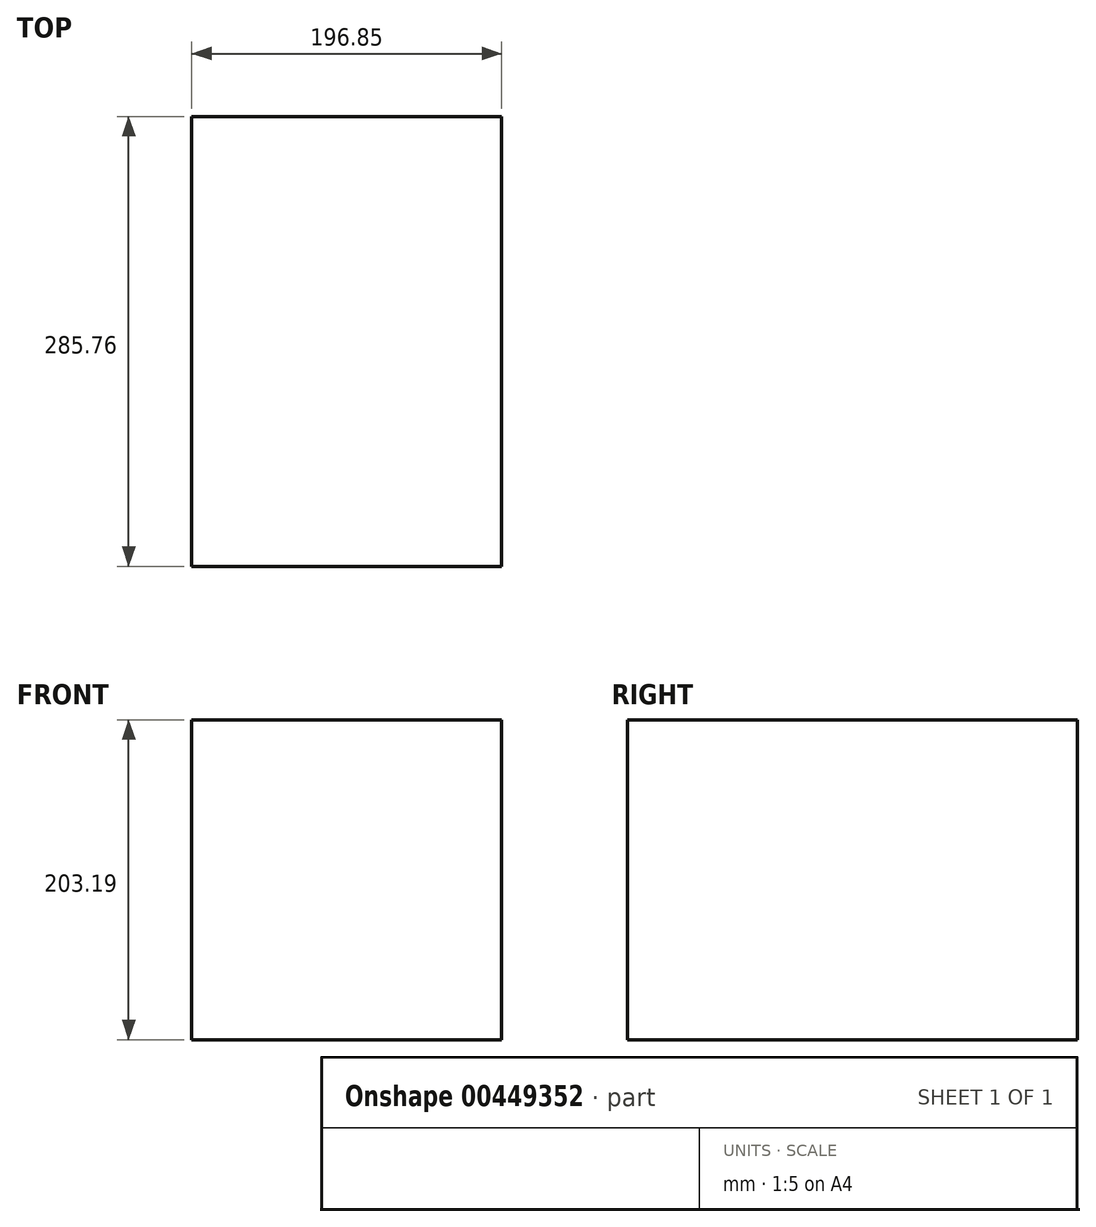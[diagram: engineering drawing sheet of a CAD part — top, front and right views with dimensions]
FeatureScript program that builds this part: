
annotation { "Feature Type Name" : "Feature", "Feature Type Description" : "" }
export const myFeature = defineFeature(function(context is Context, id is Id, definition is map)
    precondition{}
    {
        {
            var Q0;
            Q0=qCreatedBy(makeId("Front.planeOp"),FACE);
            var sketch = newSketch(context, id + "F0", { "sketchPlane" : qUnion([Q0])});
            skLineSegment(sketch, "E0.bottom", {"start": v(-92.08, 98.42) * mm, "end": v(104.78, 98.42) * mm});
            skLineSegment(sketch, "E0.top", {"start": v(-92.08, -104.78) * mm, "end": v(104.78, -104.78) * mm});
            skLineSegment(sketch, "E0.left", {"start": v(-92.08, 98.42) * mm, "end": v(-92.08, -104.78) * mm});
            skLineSegment(sketch, "E0.right", {"start": v(104.78, 98.42) * mm, "end": v(104.78, -104.78) * mm});
            skSolve(sketch);
        }
        {
            var Q0;
            Q0=makeQuery(id+"F0.imprint","IMPRINT",FACE,{"disambiguationData":[TD([[makeQuery(id+"F0.imprint","IMPRINT",EDGE,{"derivedFrom":sQuery(id+"F0.wireOp",EDGE,"E0.bottom")}),-1.0]])]});
            extrude(context, id + "F1", {"entities" : qUnion([Q0]), "depth" : 285.75 * mm, "symmetric" : true});
        }
    });
